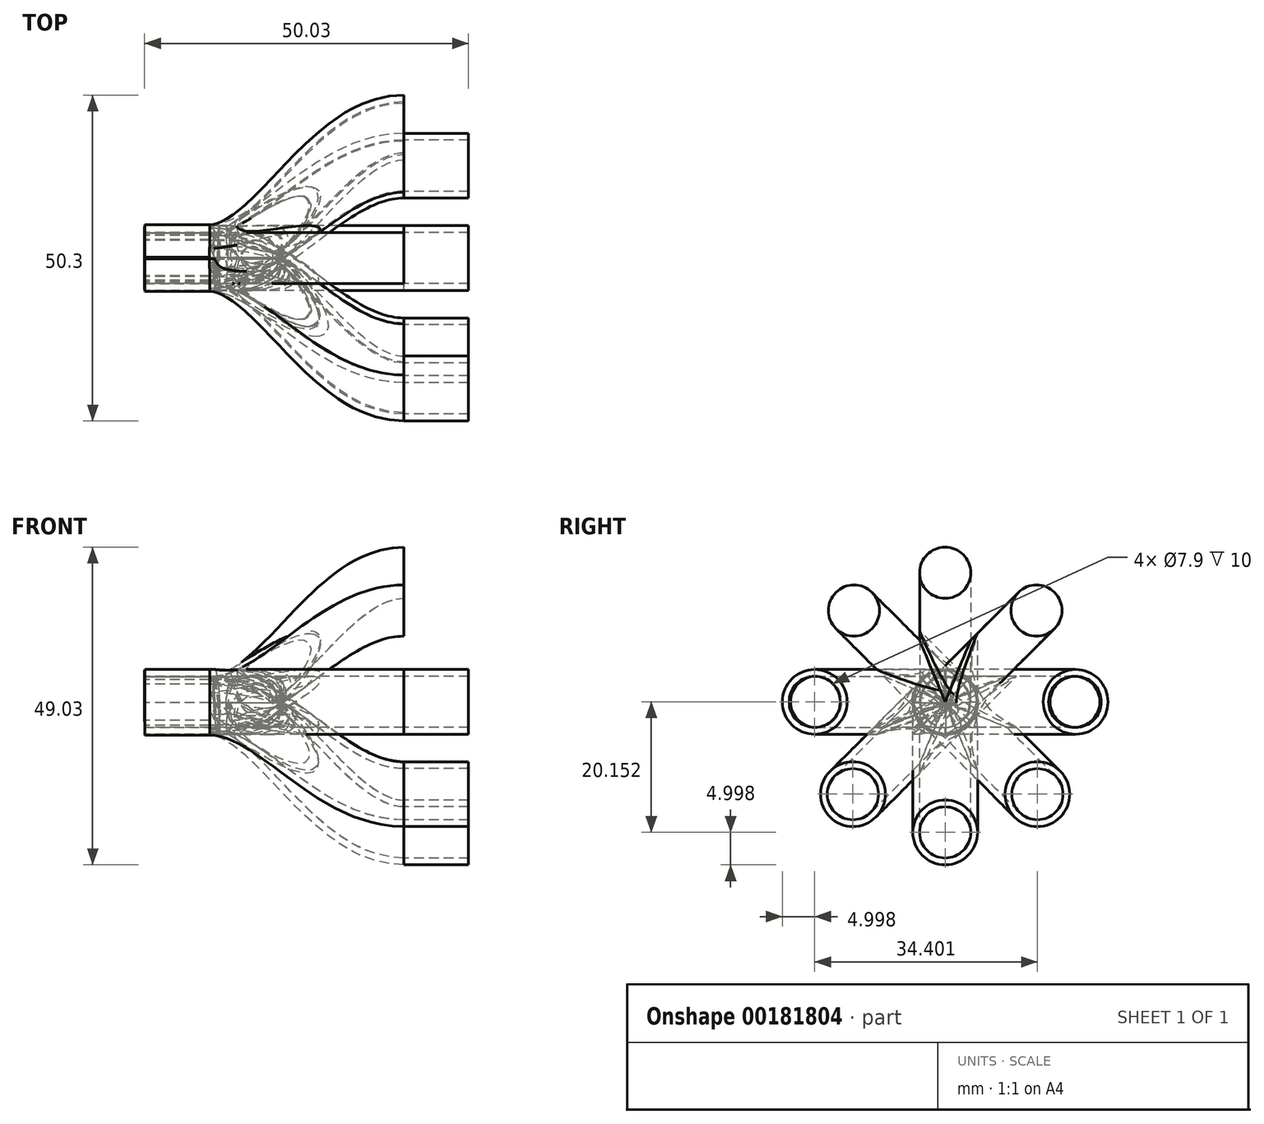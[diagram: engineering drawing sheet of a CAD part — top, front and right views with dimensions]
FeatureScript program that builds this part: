
annotation { "Feature Type Name" : "Feature", "Feature Type Description" : "" }
export const myFeature = defineFeature(function(context is Context, id is Id, definition is map)
    precondition{}
    {
        {
            var Q0;
            Q0=qCreatedBy(makeId("Top.planeOp"),FACE);
            var sketch = newSketch(context, id + "F0", { "sketchPlane" : qUnion([Q0])});
            skLineSegment(sketch, "E0", {"start": v(0, 20) * mm, "end": v(0, -20) * mm, "construction": true});
            skLineSegment(sketch, "E1", {"start": v(0, 0) * mm, "end": v(-30, 0) * mm, "construction": true});
            skFitSpline(sketch, "E2", {"points": [v(0, 20) * mm, v(-30, 0) * mm], "startDerivative": vector(-34.93, -0.21) * mm, "endDerivative": vector(-31.02, 0) * mm});
            skFitSpline(sketch, "E3.MirrorCS", {"points": [v(0, -20) * mm, v(-30, 0) * mm], "startDerivative": vector(-34.93, 0.21) * mm, "endDerivative": vector(-31.02, 0) * mm});
            skLineSegment(sketch, "E4", {"start": v(-30, 0) * mm, "end": v(-40, 0) * mm});
            skSolve(sketch);
        }
        {
            var Q0;
            Q0=qCreatedBy(makeId("Right.planeOp"),FACE);
            var sketch = newSketch(context, id + "F1", { "sketchPlane" : qUnion([Q0])});
            skCircle(sketch, "E5", {"center": v(20.15, 0) * mm, "radius": 5 * mm});
            skCircle(sketch, "E6", {"center": v(-19.93, 0) * mm, "radius": 5 * mm});
            skSolve(sketch);
        }
        {
            var Q0;
            Q0=makeQuery(id+"F1.imprint","IMPRINT",FACE,{"disambiguationData":[TD([[makeQuery(id+"F1.imprint","IMPRINT",EDGE,{"derivedFrom":sQuery(id+"F1.wireOp",EDGE,"E5")}),1.0]])]});
            var Q1;
            Q1=sQuery(id+"F0.wireOp",EDGE,"E2");
            var Q2;
            Q2=sQuery(id+"F0.wireOp",EDGE,"E4");
            sweep(context, id + "F2", {"profiles" : qUnion([Q0]), "path" : qUnion([Q1, Q2])});
        }
        {
            var Q0;
            Q0=makeQuery(id+"F1.imprint","IMPRINT",FACE,{"disambiguationData":[TD([[makeQuery(id+"F1.imprint","IMPRINT",EDGE,{"derivedFrom":sQuery(id+"F1.wireOp",EDGE,"E6")}),1.0]])]});
            var Q1;
            Q1=sQuery(id+"F0.wireOp",EDGE,"E3.MirrorCS");
            sweep(context, id + "F3", {"operationType" : NewBodyOperationType.ADD, "profiles" : qUnion([Q0]), "path" : qUnion([Q1])});
        }
        {
            var Q0;
            Q0=makeQuery(id+"F1.imprint","IMPRINT",FACE,{"disambiguationData":[TD([[makeQuery(id+"F1.imprint","IMPRINT",EDGE,{"derivedFrom":sQuery(id+"F1.wireOp",EDGE,"E6")}),1.0]])]});
            var sketch = newSketch(context, id + "F4", { "sketchPlane" : qUnion([Q0])});
            skCircle(sketch, "E7.0", {"center": v(-19.93, 0) * mm, "radius": 3.95 * mm});
            skCircle(sketch, "E8.0", {"center": v(20.15, 0) * mm, "radius": 3.95 * mm});
            skSolve(sketch);
        }
        {
            var Q0;
            Q0=makeQuery(id+"F4.imprint","IMPRINT",FACE,{"disambiguationData":[TD([[makeQuery(id+"F4.imprint","IMPRINT",EDGE,{"derivedFrom":sQuery(id+"F4.wireOp",EDGE,"E7.0")}),-1.0]])]});
            var Q1;
            Q1=sQuery(id+"F0.wireOp",EDGE,"E3.MirrorCS");
            var Q2;
            Q2=sQuery(id+"F0.wireOp",EDGE,"E4");
            sweep(context, id + "F5", {"operationType" : NewBodyOperationType.REMOVE, "profiles" : qUnion([Q0]), "path" : qUnion([Q1, Q2])});
        }
        {
            var Q0;
            Q0=makeQuery(id+"F4.imprint","IMPRINT",FACE,{"disambiguationData":[TD([[makeQuery(id+"F4.imprint","IMPRINT",EDGE,{"derivedFrom":sQuery(id+"F4.wireOp",EDGE,"E8.0")}),1.0]])]});
            var Q1;
            Q1=sQuery(id+"F0.wireOp",EDGE,"E2");
            var Q2;
            Q2=sQuery(id+"F0.wireOp",EDGE,"E4");
            sweep(context, id + "F6", {"operationType" : NewBodyOperationType.REMOVE, "profiles" : qUnion([Q0]), "path" : qUnion([Q1, Q2])});
        }
        {
            var Q0;
            Q0=makeQuery(id+"F2.opSweep","SWEPT_BODY",BODY,{"disambiguationData":[OSD([sQuery(id+"F0.wireOp",EDGE,"E4"),sQuery(id+"F1.wireOp",EDGE,"E5")])]});
            var Q1;
            Q1=sQuery(id+"F0.wireOp",EDGE,"E4");
            circularPattern(context, id + "F7", {"entities" : qUnion([Q0]), "axis" : qUnion([Q1]), "angle" : 45 * degree, "instanceCount" : 4});
        }
        {
            var Q0;
            Q0=makeQuery(id+"F4.imprint","IMPRINT",FACE,{"disambiguationData":[TD([[makeQuery(id+"F4.imprint","IMPRINT",EDGE,{"derivedFrom":sQuery(id+"F4.wireOp",EDGE,"E8.0")}),1.0]])]});
            var Q1;
            Q1=sQuery(id+"F0.wireOp",EDGE,"E2");
            sweep(context, id + "F8", {"operationType" : NewBodyOperationType.REMOVE, "profiles" : qUnion([Q0]), "path" : qUnion([Q1])});
        }
        {
            var Q0;
            Q0=makeQuery(id+"F4.imprint","IMPRINT",FACE,{"disambiguationData":[TD([[makeQuery(id+"F4.imprint","IMPRINT",EDGE,{"derivedFrom":sQuery(id+"F4.wireOp",EDGE,"E7.0")}),-1.0]])]});
            var Q1;
            Q1=sQuery(id+"F0.wireOp",EDGE,"E3.MirrorCS");
            sweep(context, id + "F9", {"operationType" : NewBodyOperationType.REMOVE, "profiles" : qUnion([Q0]), "path" : qUnion([Q1])});
        }
        {
            var Q0;
            Q0=makeQuery(id+"F7.opPattern","COPY",FACE,{"derivedFrom":makeQuery(id+"F2.opSweep","CAP_FACE",FACE,{"disambiguationData":[OSD([sQuery(id+"F0.wireOp",VERTEX,"E2.start"),sQuery(id+"F1.wireOp",EDGE,"E5")])],"isStart":true}),"instanceName":"1"});
            var sketch = newSketch(context, id + "F10", { "sketchPlane" : qUnion([Q0])});
            skCircle(sketch, "E9.0", {"center": v(14.25, -14.25) * mm, "radius": 5 * mm});
            skCircle(sketch, "E10.0", {"center": v(14.25, -14.25) * mm, "radius": 3.95 * mm});
            skSolve(sketch);
        }
        {
            var Q0;
            Q0=qSketchRegion(id+"F10",true);
            extrude(context, id + "F11", {"entities" : qUnion([Q0]), "operationType" : NewBodyOperationType.ADD, "depth" : 10 * mm});
        }
        {
            var Q0;
            Q0=makeQuery(id+"F7.opPattern","COPY",BODY,{"derivedFrom":makeQuery(id+"F2.opSweep","SWEPT_BODY",BODY,{"disambiguationData":[OSD([sQuery(id+"F0.wireOp",EDGE,"E4"),sQuery(id+"F1.wireOp",EDGE,"E5")])]}),"instanceName":"1"});
            var Q1;
            Q1=sQuery(id+"F0.wireOp",EDGE,"E4");
            circularPattern(context, id + "F12", {"entities" : qUnion([Q0]), "axis" : qUnion([Q1]), "angle" : 45 * degree, "instanceCount" : 4});
        }
    });
